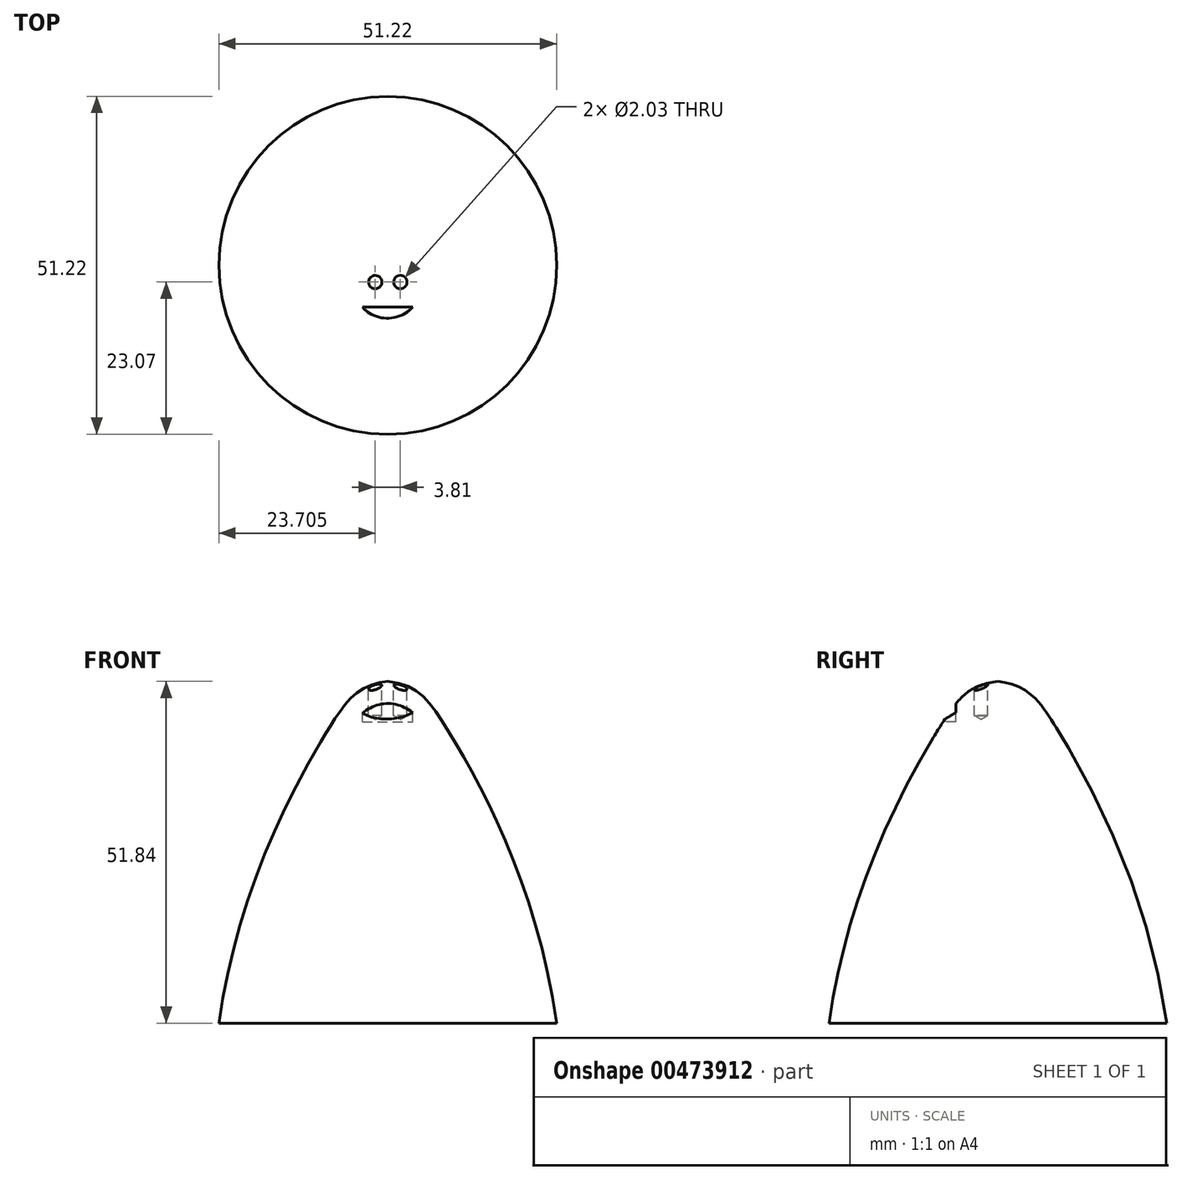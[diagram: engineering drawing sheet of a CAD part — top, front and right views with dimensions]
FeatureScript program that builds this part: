
annotation { "Feature Type Name" : "Feature", "Feature Type Description" : "" }
export const myFeature = defineFeature(function(context is Context, id is Id, definition is map)
    precondition{}
    {
        {
            var Q0;
            Q0=qCreatedBy(makeId("Front.planeOp"),FACE);
            var sketch = newSketch(context, id + "F0", { "sketchPlane" : qUnion([Q0])});
            skLineSegment(sketch, "E0", {"start": v(0, 0) * mm, "end": v(0, 51.84) * mm});
            skLineSegment(sketch, "E1", {"start": v(0, 0) * mm, "end": v(25.61, 0) * mm});
            skFitSpline(sketch, "E2", {"points": [v(25.61, 0) * mm, v(8.63, 45.19) * mm, v(0, 51.84) * mm], "startDerivative": vector(-12.43, 90.76) * mm, "endDerivative": vector(-41.63, 4.53) * mm});
            skSolve(sketch);
        }
        {
            var Q0;
            Q0=makeQuery(id+"F0.imprint","IMPRINT",FACE,{"disambiguationData":[TD([[makeQuery(id+"F0.imprint","IMPRINT",EDGE,{"derivedFrom":sQuery(id+"F0.wireOp",EDGE,"E0")}),-1.0]])]});
            var Q1;
            Q1=sQuery(id+"F0.wireOp",EDGE,"E0");
            revolve(context, id + "F1", {"entities" : qUnion([Q0]), "axis" : qUnion([Q1]), "revolveType" : RevolveType.FULL});
        }
        {
            var Q0;
            Q0=qCreatedBy(makeId("Top.planeOp"),FACE);
            cPlane(context, id + "F2", {"entities" : qUnion([Q0]), "cplaneType" : CPlaneType.OFFSET, "offset" : 63.5 * mm, "width" : 152.4 * mm, "height" : 152.4 * mm});
        }
        {
            var Q0;
            Q0=qCreatedBy(id+"F2.planeOp",FACE);
            var sketch = newSketch(context, id + "F3", { "sketchPlane" : qUnion([Q0])});
            skPoint(sketch, "E3", {"position": v(-1.9, -2.54) * mm});
            skPoint(sketch, "E4", {"position": v(1.9, -2.54) * mm});
            skLineSegment(sketch, "E5", {"start": v(-3.86, -6.35) * mm, "end": v(3.76, -6.35) * mm});
            skArc(sketch, "E6", {"start": v(-3.86, -6.35) * mm, "mid": v(-0.05, -8.04) * mm, "end": v(3.76, -6.35) * mm});
            skArc(sketch, "E7", {"start": v(-0.82, -9.63) * mm, "mid": v(-2.25, -9.55) * mm, "end": v(-3.59, -10.06) * mm});
            skArc(sketch, "E8", {"start": v(1.77, -10.06) * mm, "mid": v(0.53, -9.56) * mm, "end": v(-0.82, -9.63) * mm});
            skArc(sketch, "E9", {"start": v(-4.04, -9.63) * mm, "mid": v(-3.96, -10) * mm, "end": v(-3.59, -10.06) * mm});
            skArc(sketch, "E10", {"start": v(-2.15, -8.5) * mm, "mid": v(-3.25, -8.8) * mm, "end": v(-4.04, -9.63) * mm});
            skSolve(sketch);
        }
        {
            var Q0;
            Q0=sQuery(id+"F3.wireOp",VERTEX,"E3");
            var Q1;
            Q1=sQuery(id+"F3.wireOp",VERTEX,"E4");
            var Q2;
            Q2=makeQuery(id+"F1.opRevolve","SWEPT_BODY",BODY,{"disambiguationData":[OSD([sQuery(id+"F0.wireOp",EDGE,"E0"),sQuery(id+"F0.wireOp",EDGE,"E1"),sQuery(id+"F0.wireOp",EDGE,"E2")])]});
            hole(context, id + "F4", {"style" : HoleStyle.SIMPLE, "endStyle" : HoleEndStyle.BLIND, "holeDiameter" : 2.03 * mm, "holeDepth" : 3.8 * mm, "isTappedThrough" : true, "tappedDepth" : 12.7 * mm, "tapClearance" : 3, "locations" : qUnion([Q0, Q1]), "scope" : qUnion([Q2])});
        }
        {
            var Q0;
            Q0=makeQuery(id+"F3.imprint","IMPRINT",FACE,{"disambiguationData":[TD([[makeQuery(id+"F3.imprint","IMPRINT",EDGE,{"derivedFrom":sQuery(id+"F3.wireOp",EDGE,"E5")}),-1.0]])]});
            extrude(context, id + "F5", {"entities" : qUnion([Q0]), "operationType" : NewBodyOperationType.REMOVE, "oppositeDirection" : true, "depth" : 17.78 * mm});
        }
    });
